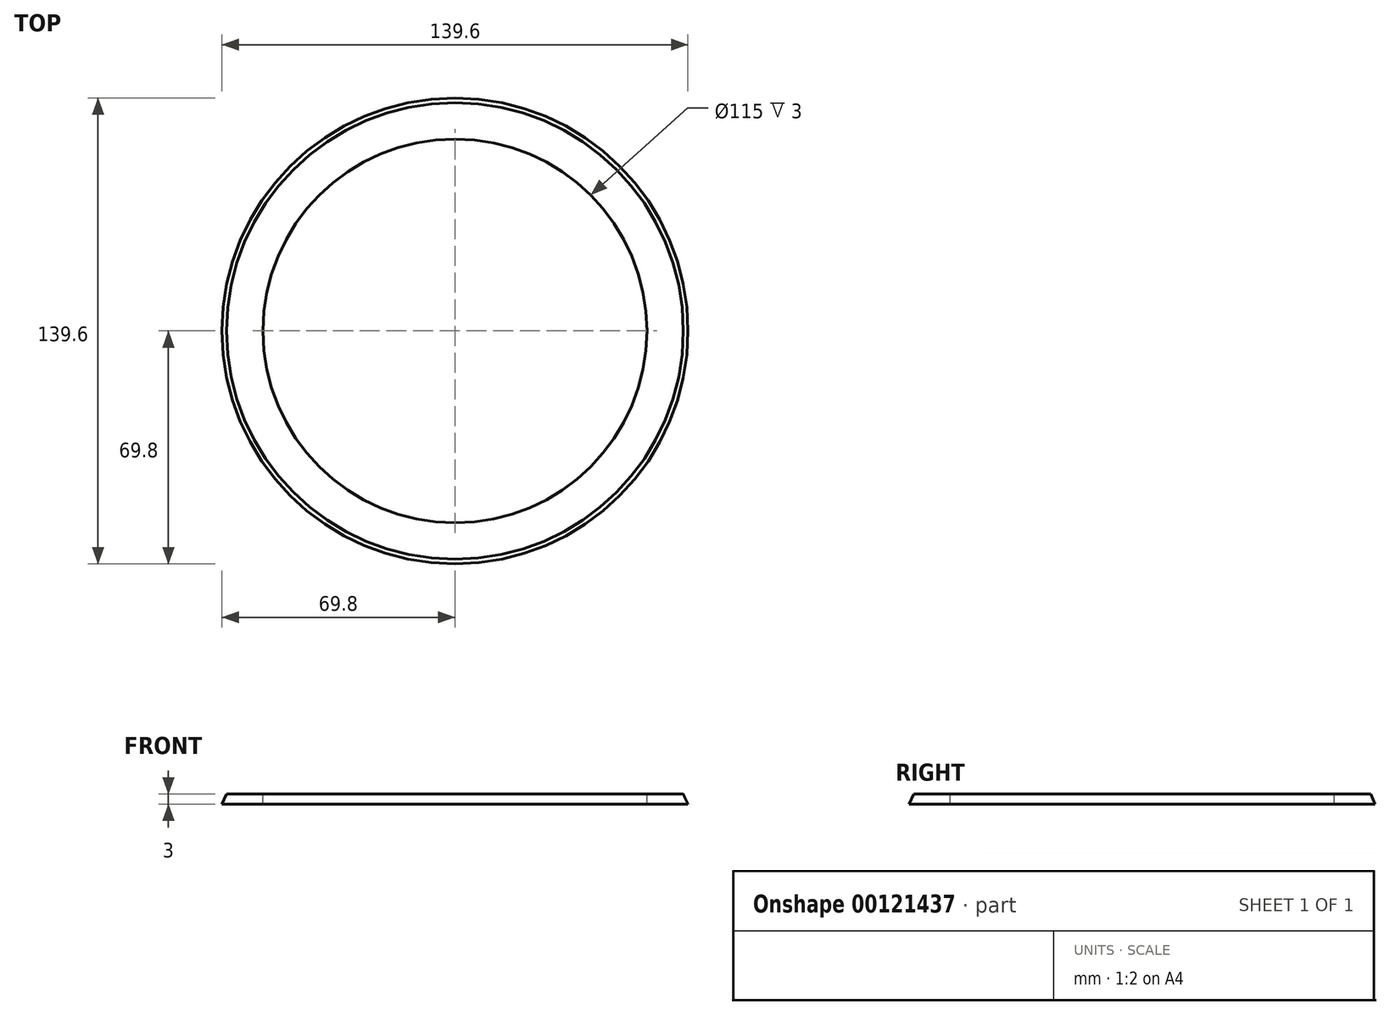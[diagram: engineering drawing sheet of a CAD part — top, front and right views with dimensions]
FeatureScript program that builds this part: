
annotation { "Feature Type Name" : "Feature", "Feature Type Description" : "" }
export const myFeature = defineFeature(function(context is Context, id is Id, definition is map)
    precondition{}
    {
        {
            var Q0;
            Q0=qCreatedBy(makeId("Front.planeOp"),FACE);
            var sketch = newSketch(context, id + "F0", { "sketchPlane" : qUnion([Q0])});
            skLineSegment(sketch, "E0.0", {"start": v(68.41, 3) * mm, "end": v(69.8, 0) * mm});
            skPoint(sketch, "E1.end.orphan", {"position": v(-60.33, 25.25) * mm});
            skPoint(sketch, "E2.orphan", {"position": v(-72, 0) * mm});
            skLineSegment(sketch, "E3", {"start": v(69.8, 0) * mm, "end": v(0, 0) * mm});
            skLineSegment(sketch, "E4.0", {"start": v(68.41, 3) * mm, "end": v(0, 3) * mm});
            skLineSegment(sketch, "E5", {"start": v(0, 3) * mm, "end": v(0, 0) * mm});
            skSolve(sketch);
        }
        {
            var Q0;
            Q0 = qSketchRegion(id + "F0", true);
            var Q1;
            Q1=sQuery(id+"F0.wireOp",EDGE,"E5");
            revolve(context, id + "F1", {"entities" : qUnion([Q0]), "axis" : qUnion([Q1]), "revolveType" : RevolveType.FULL});
        }
        {
            var Q0;
            Q0=makeQuery(id+"F1.opRevolve","SWEPT_FACE",FACE,{"disambiguationData":[OSD([sQuery(id+"F0.wireOp",EDGE,"E4.0")])]});
            var sketch = newSketch(context, id + "F2", { "sketchPlane" : qUnion([Q0])});
            skCircle(sketch, "E6", {"center": v(0, 0) * mm, "radius": 57.5 * mm});
            skSolve(sketch);
        }
        {
            var Q0;
            Q0=makeQuery(id+"F2.imprint","IMPRINT",FACE,{"disambiguationData":[TD([[makeQuery(id+"F2.imprint","IMPRINT",EDGE,{"derivedFrom":sQuery(id+"F2.wireOp",EDGE,"E6")}),1.0]])]});
            extrude(context, id + "F3", {"entities" : qUnion([Q0]), "operationType" : NewBodyOperationType.REMOVE, "oppositeDirection" : true, "depth" : 3 * mm});
        }
    });
